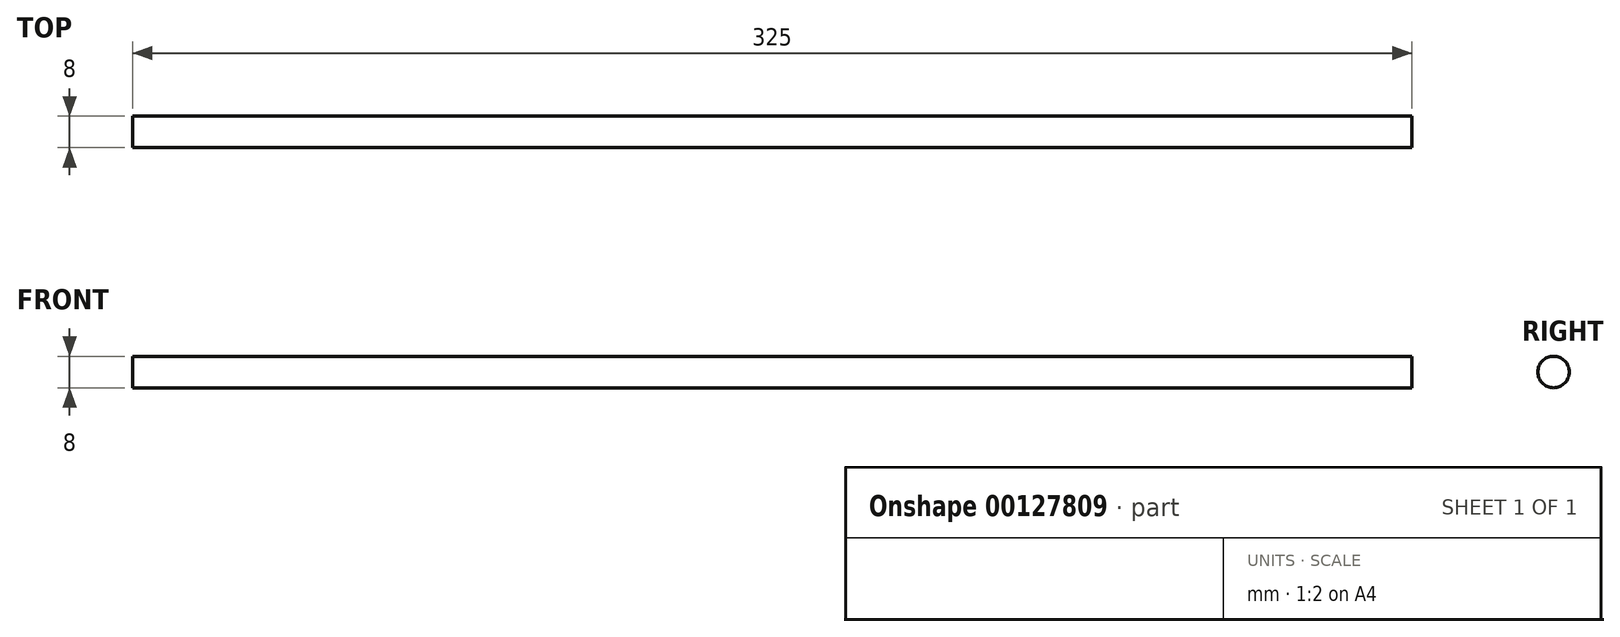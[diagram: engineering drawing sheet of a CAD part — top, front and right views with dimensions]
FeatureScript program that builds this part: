
annotation { "Feature Type Name" : "Feature", "Feature Type Description" : "" }
export const myFeature = defineFeature(function(context is Context, id is Id, definition is map)
    precondition{}
    {
        {
            var Q0;
            Q0=qCreatedBy(makeId("Right.planeOp"),FACE);
            var sketch = newSketch(context, id + "F0", { "sketchPlane" : qUnion([Q0])});
            skCircle(sketch, "E0", {"center": v(0, 0) * mm, "radius": 4 * mm});
            skSolve(sketch);
        }
        {
            var Q0;
            Q0 = qSketchRegion(id + "F0", true);
            extrude(context, id + "F1", {"entities" : qUnion([Q0]), "endBound" : BoundingType.SYMMETRIC, "depth" : 325 * mm});
        }
    });
